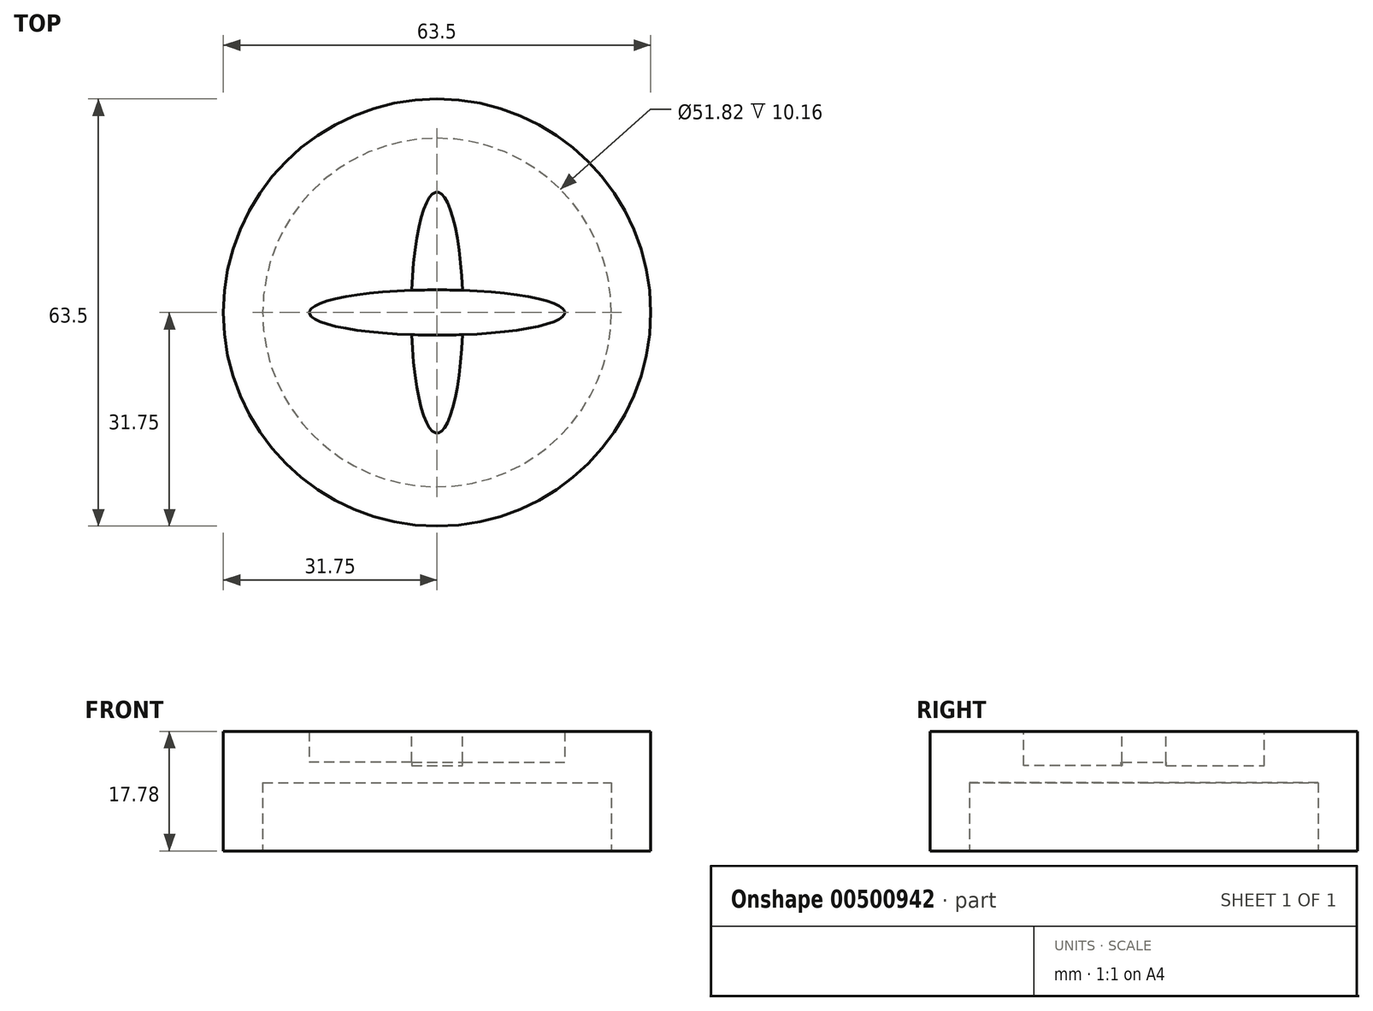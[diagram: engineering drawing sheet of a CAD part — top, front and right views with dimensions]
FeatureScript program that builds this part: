
annotation { "Feature Type Name" : "Feature", "Feature Type Description" : "" }
export const myFeature = defineFeature(function(context is Context, id is Id, definition is map)
    precondition{}
    {
        {
            var Q0;
            Q0=qCreatedBy(makeId("Top.planeOp"),FACE);
            var sketch = newSketch(context, id + "F0", { "sketchPlane" : qUnion([Q0])});
            skCircle(sketch, "E0", {"center": v(0, 0) * mm, "radius": 31.75 * mm});
            skSolve(sketch);
        }
        {
            var Q0;
            Q0=makeQuery(id+"F0.imprint","IMPRINT",FACE,{"disambiguationData":[TD([[makeQuery(id+"F0.imprint","IMPRINT",EDGE,{"derivedFrom":sQuery(id+"F0.wireOp",EDGE,"E0")}),1.0]])]});
            extrude(context, id + "F1", {"entities" : qUnion([Q0]), "depth" : 17.78 * mm});
        }
        {
            var Q0;
            Q0=makeQuery(id+"F1.opExtrude","CAP_FACE",FACE,{"disambiguationData":[OSD([sQuery(id+"F0.wireOp",EDGE,"E0")])],"isStart":true});
            var sketch = newSketch(context, id + "F2", { "sketchPlane" : qUnion([Q0])});
            skCircle(sketch, "E1", {"center": v(0, 0) * mm, "radius": 25.9 * mm});
            skSolve(sketch);
        }
        {
            var Q0;
            Q0 = qSketchRegion(id + "F2", true);
            extrude(context, id + "F3", {"entities" : qUnion([Q0]), "operationType" : NewBodyOperationType.REMOVE, "oppositeDirection" : true, "depth" : 10.16 * mm});
        }
        {
            var Q0;
            Q0=makeQuery(id+"F1.opExtrude","CAP_FACE",FACE,{"disambiguationData":[OSD([sQuery(id+"F0.wireOp",EDGE,"E0")])],"isStart":false});
            var sketch = newSketch(context, id + "F4", { "sketchPlane" : qUnion([Q0])});
            skEllipse(sketch, "E2", {"center": v(0, 0) * mm, "majorRadius": 18.98 * mm, "minorRadius": 3.36 * mm, "majorAxis": v(-1, 0)});
            skSolve(sketch);
        }
        {
            var Q0;
            Q0=makeQuery(id+"F4.imprint","IMPRINT",FACE,{"disambiguationData":[TD([[makeQuery(id+"F4.imprint","IMPRINT",EDGE,{"derivedFrom":sQuery(id+"F4.wireOp",EDGE,"E2")}),1.0]])]});
            var Q1;
            Q1=sQuery(id+"F4.wireOp",EDGE,"E2");
            extrude(context, id + "F5", {"entities" : qUnion([Q0]), "operationType" : NewBodyOperationType.REMOVE, "surfaceEntities" : qUnion([Q1]), "oppositeDirection" : true, "depth" : 4.57 * mm, "offsetDistance" : 25.4 * mm});
        }
        {
            var Q0;
            Q0=makeQuery(id+"F1.opExtrude","CAP_FACE",FACE,{"disambiguationData":[OSD([sQuery(id+"F0.wireOp",EDGE,"E0")])],"isStart":false});
            var sketch = newSketch(context, id + "F6", { "sketchPlane" : qUnion([Q0])});
            skEllipse(sketch, "E3", {"center": v(0, 0) * mm, "majorRadius": 17.9 * mm, "minorRadius": 3.83 * mm, "majorAxis": v(0, 1)});
            skSolve(sketch);
        }
        {
            var Q0;
            {var subQ0=sQuery(id+"F6.wireOp",EDGE,"E3");var subQ1=makeQuery(id+"F5.boolean.opBoolean","COPY",EDGE,{"derivedFrom":makeQuery(id+"F5.opExtrude","CAP_EDGE",EDGE,{"disambiguationData":[OSD([sQuery(id+"F4.wireOp",EDGE,"E2")])],"isStart":true})});var subQ2=makeQuery(id+"F6.imprint","INTERSECT",VERTEX,{"disambiguationData":[OD(1.0)],"derivedFrom":[subQ1,subQ0]});Q0=makeQuery(id+"F6.imprint","IMPRINT",FACE,{"disambiguationData":[TD([[makeQuery(id+"F6.imprint","IMPRINT",EDGE,{"disambiguationData":[TD([[subQ2,1.0]])],"derivedFrom":subQ0}),1.0]])]});}
            var Q1;
            {var subQ0=sQuery(id+"F6.wireOp",EDGE,"E3");var subQ1=makeQuery(id+"F5.boolean.opBoolean","COPY",EDGE,{"derivedFrom":makeQuery(id+"F5.opExtrude","CAP_EDGE",EDGE,{"disambiguationData":[OSD([sQuery(id+"F4.wireOp",EDGE,"E2")])],"isStart":true})});var subQ2=makeQuery(id+"F6.imprint","INTERSECT",VERTEX,{"disambiguationData":[OD(0.0)],"derivedFrom":[subQ1,subQ0]});Q1=makeQuery(id+"F6.imprint","IMPRINT",FACE,{"disambiguationData":[TD([[makeQuery(id+"F6.imprint","IMPRINT",EDGE,{"disambiguationData":[TD([[subQ2,-1.0]])],"derivedFrom":subQ0}),1.0]])]});}
            var Q2;
            Q2=sQuery(id+"F6.wireOp",EDGE,"E3");
            extrude(context, id + "F7", {"entities" : qUnion([Q0, Q1]), "operationType" : NewBodyOperationType.REMOVE, "surfaceEntities" : qUnion([Q2]), "oppositeDirection" : true, "depth" : 5.08 * mm, "offsetDistance" : 25.4 * mm});
        }
    });
